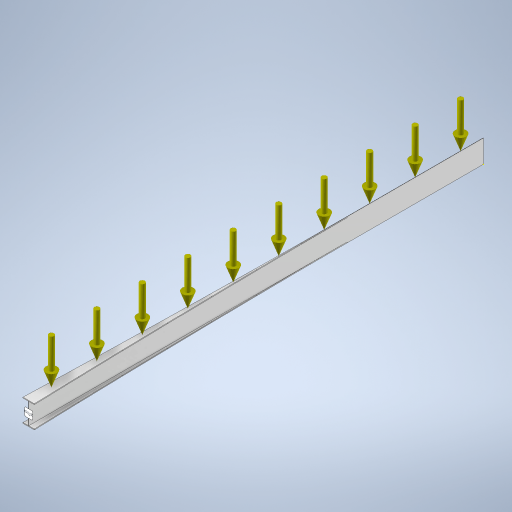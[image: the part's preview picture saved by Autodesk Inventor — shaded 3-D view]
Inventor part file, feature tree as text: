
AUTODESK INVENTOR PART (.ipt)
format: ipt  version: 2024 (Build 280153000, 153)  size: 417,792 bytes
history: native  units: mm
features: sketch x4, extrude x3, split x1, mirror x1, pattern_linear x1
ambient origin geometry x8: Origin, YZ Plane, XZ Plane, XY Plane, X Axis, Y Axis, Z Axis, Center Point
bodies: Solid1 (feature_tree)
feature tree (10):
  sketch  "Sketch1"  dims[d0=100.0mm d1=2.0mm]
  extrude  "Extrusion1"  Depth=2.0mm
  extrude  "Extrusion4"  Depth=7.589mm
  split  "Split1"
  mirror  "Mirror1"
  extrude  "Extrusion5"  Depth=4000.0mm TaperAngle=0.0deg
  pattern_linear  "Rectangular Pattern1"  Count1=40  [1 undecoded]
  sketch  "Sketch2"  dims[d2=7.589mm d3=7.589mm]
  sketch  "Sketch5"  dims[d4=200.0mm d5=4000.0mm d6=0.0mm d23=400.0mm]
  sketch  "Sketch6"  dims[d25=400.0mm d27=400.0mm d28=30.75mm d29=400.0mm d30=37.9mm d31=11.85mm d32=22.1mm d33=400.0mm d34=400.0mm d35=43.55mm d37=400.0mm d38=400.0mm d39=400.0mm d40=400.0mm d43=47.85mm d44=49.0mm d45=49.0mm d46=49.0mm d47=49.0mm d48=1000.0mm d49=0.0mm d50=200.0mm d51=1.0mm d52=0.001mm d53=0.0mm d54=100.0mm d56=400.0mm d7=0.5mm d8=0.872665mm d17=0.5mm d18=0.872665mm d19=0.5mm d20=0.872665mm d41=0.5mm d42=0.872665mm]
note: 1 required parameter value undecoded (feature->parameter linkage not recoverable at this tier; creation-order binding heuristic only, values carry confidence <= 0.55)
